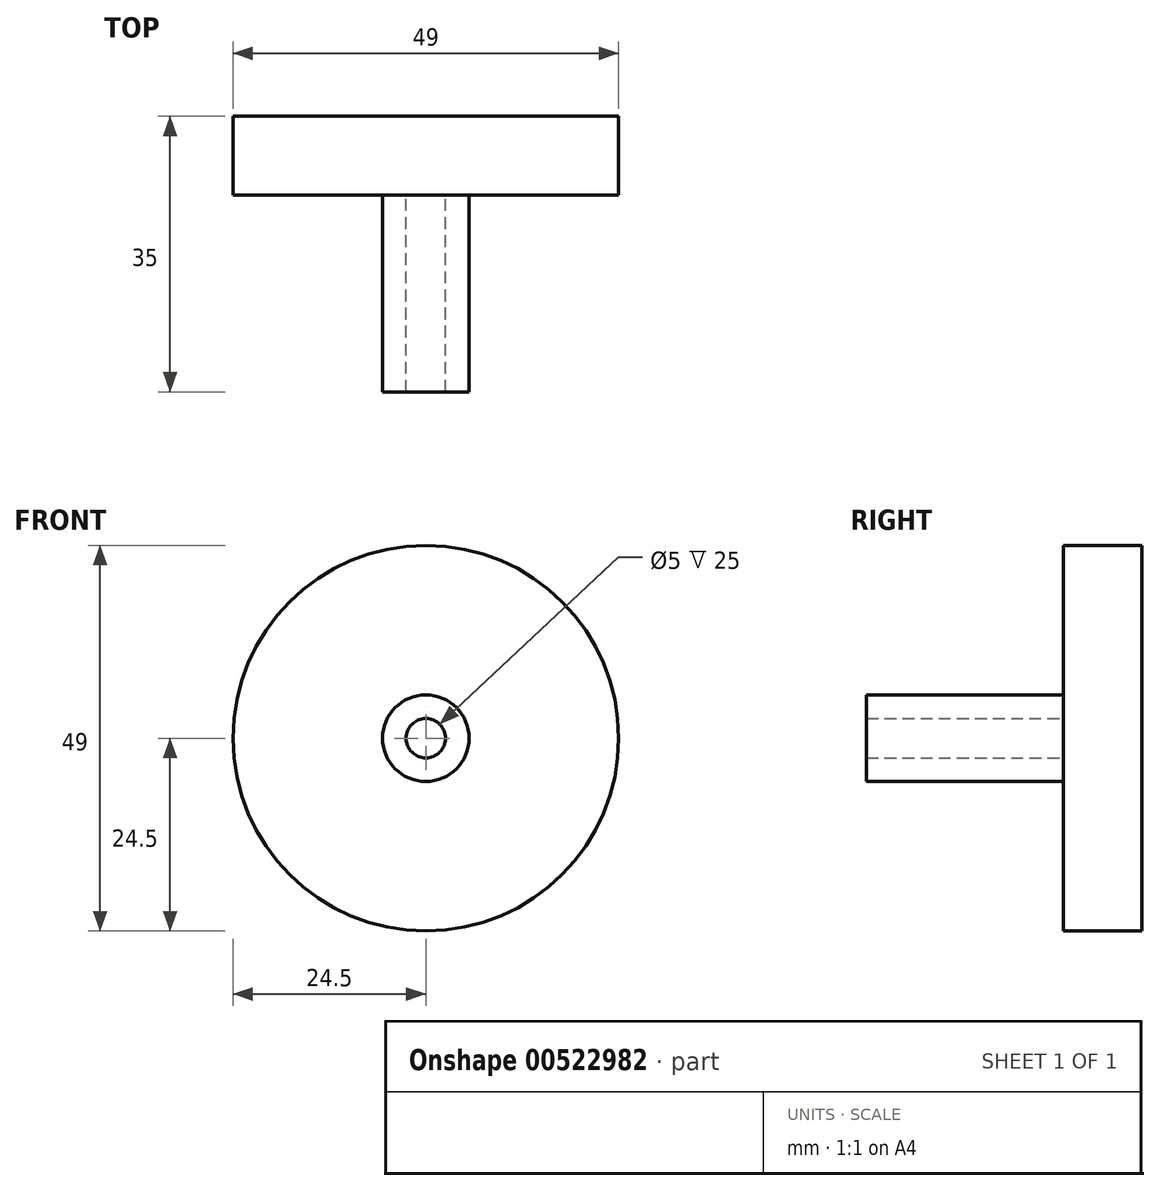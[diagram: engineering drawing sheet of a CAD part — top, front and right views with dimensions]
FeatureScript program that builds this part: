
annotation { "Feature Type Name" : "Feature", "Feature Type Description" : "" }
export const myFeature = defineFeature(function(context is Context, id is Id, definition is map)
    precondition{}
    {
        {
            var Q0;
            Q0=qCreatedBy(makeId("Front.planeOp"),FACE);
            var sketch = newSketch(context, id + "F0", { "sketchPlane" : qUnion([Q0])});
            skCircle(sketch, "E0", {"center": v(0, 0) * mm, "radius": 24.5 * mm});
            skSolve(sketch);
        }
        {
            var Q0;
            Q0 = qSketchRegion(id + "F0", true);
            extrude(context, id + "F1", {"entities" : qUnion([Q0]), "endBound" : BoundingType.SYMMETRIC, "depth" : 10 * mm, "offsetDistance" : 25 * mm});
        }
        {
            var Q0;
            Q0=qCreatedBy(makeId("Front.planeOp"),FACE);
            var sketch = newSketch(context, id + "F2", { "sketchPlane" : qUnion([Q0])});
            skCircle(sketch, "E1", {"center": v(0, 0) * mm, "radius": 5.5 * mm});
            skCircle(sketch, "E2", {"center": v(0, 0) * mm, "radius": 2.5 * mm});
            skSolve(sketch);
        }
        {
            var Q0;
            Q0 = qSketchRegion(id + "F2", true);
            extrude(context, id + "F3", {"entities" : qUnion([Q0]), "operationType" : NewBodyOperationType.ADD, "depth" : 30 * mm, "offsetDistance" : 25 * mm});
        }
    });
